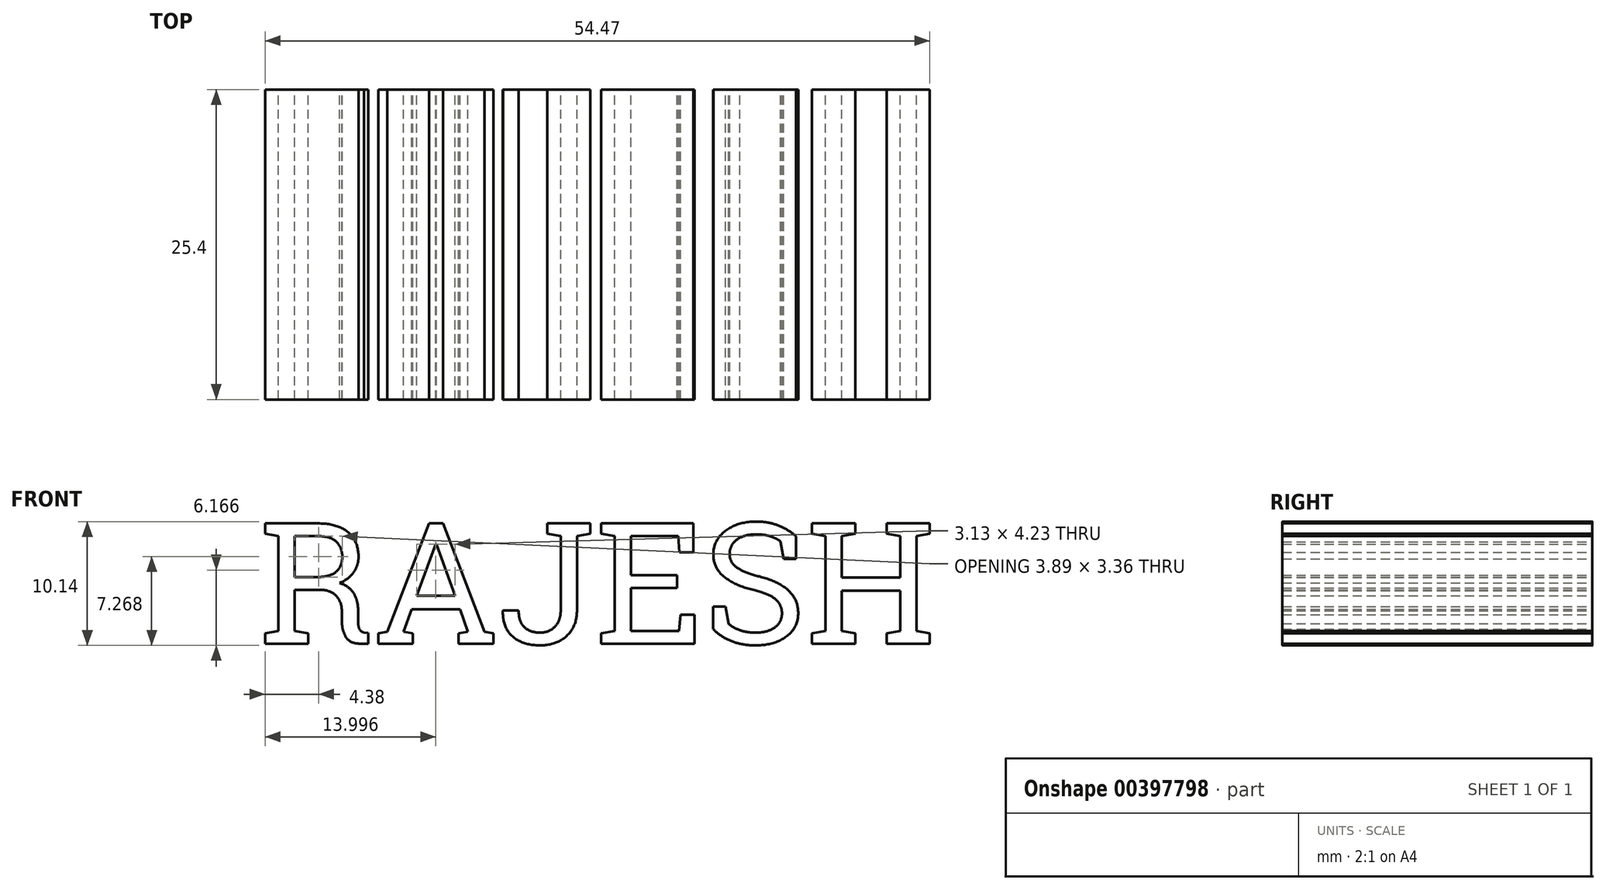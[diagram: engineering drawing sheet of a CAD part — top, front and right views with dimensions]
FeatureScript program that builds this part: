
annotation { "Feature Type Name" : "Feature", "Feature Type Description" : "" }
export const myFeature = defineFeature(function(context is Context, id is Id, definition is map)
    precondition{}
    {
        {
            var Q0;
            Q0=qCreatedBy(makeId("Front.planeOp"),FACE);
            var sketch = newSketch(context, id + "F0", { "sketchPlane" : qUnion([Q0])});
            skText(sketch, "E0", { "text": "RAJESH", "fontName": "RobotoSlab-Regular.ttf"});
            const initialGuessF0  = {"E0": [-0.0267, 0.00499, 1, 0, 0.00998]};
            skSetInitialGuess(sketch, initialGuessF0);
            skSolve(sketch);
        }
        {
            var Q0;
            Q0 = qSketchRegion(id + "F0", true);
            extrude(context, id + "F1", {"entities" : qUnion([Q0]), "depth" : 25.4 * mm});
        }
    });
